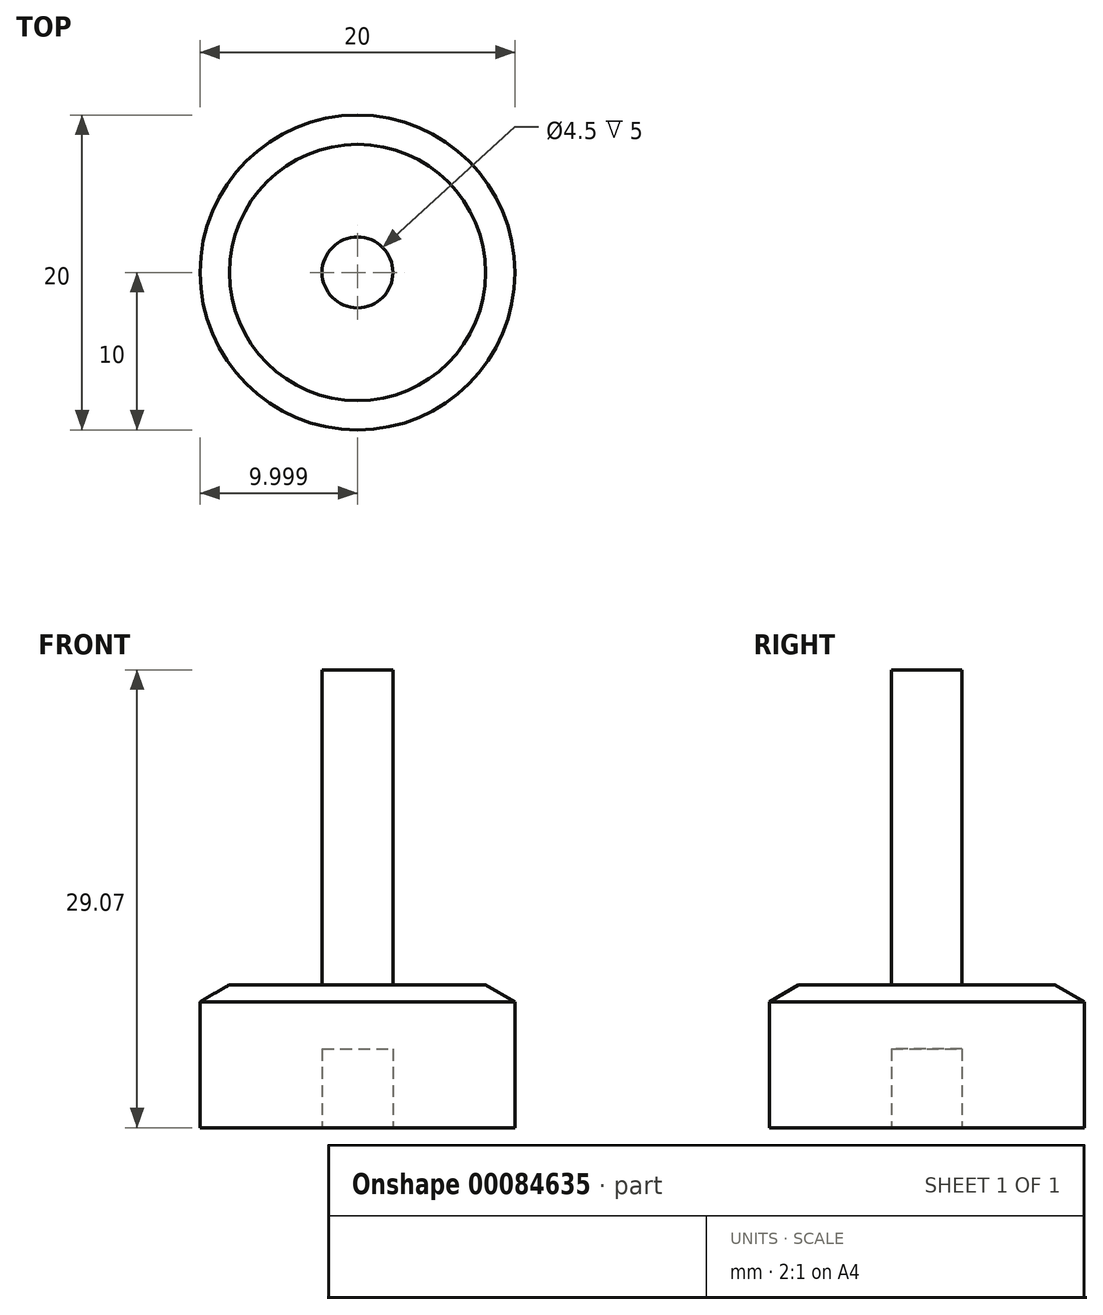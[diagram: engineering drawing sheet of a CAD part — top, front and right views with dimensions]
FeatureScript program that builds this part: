
annotation { "Feature Type Name" : "Feature", "Feature Type Description" : "" }
export const myFeature = defineFeature(function(context is Context, id is Id, definition is map)
    precondition{}
    {
        {
            var Q0;
            Q0=qCreatedBy(makeId("Front.planeOp"),FACE);
            var sketch = newSketch(context, id + "F0", { "sketchPlane" : qUnion([Q0])});
            skLineSegment(sketch, "E0.bottom", {"start": v(-30.55, 8) * mm, "end": v(-20.55, 8) * mm});
            skLineSegment(sketch, "E0.top", {"start": v(-30.55, 0) * mm, "end": v(-22.8, 0) * mm});
            skLineSegment(sketch, "E0.left", {"start": v(-30.55, 8) * mm, "end": v(-30.55, 0) * mm});
            skPoint(sketch, "E1", {"position": v(-20.55, 8) * mm});
            skPoint(sketch, "E2", {"position": v(-20.55, 0) * mm});
            skPoint(sketch, "E3", {"position": v(-20.55, 9.07) * mm});
            skLineSegment(sketch, "E4", {"start": v(-20.55, 8) * mm, "end": v(-20.55, 9.07) * mm});
            skLineSegment(sketch, "E5", {"start": v(-30.55, 8) * mm, "end": v(-28.7, 9.07) * mm});
            skLineSegment(sketch, "E6", {"start": v(-28.7, 9.07) * mm, "end": v(-20.55, 9.07) * mm});
            skLineSegment(sketch, "E7", {"start": v(-20.55, 8) * mm, "end": v(-20.55, 5) * mm});
            skPoint(sketch, "E0.right.end.orphan", {"position": v(-10.55, 0) * mm});
            skPoint(sketch, "E8.start.orphan", {"position": v(-10.55, 8) * mm});
            skLineSegment(sketch, "E9", {"start": v(-20.55, 9.07) * mm, "end": v(-20.55, 29.07) * mm});
            skLineSegment(sketch, "E10", {"start": v(-20.55, 29.07) * mm, "end": v(-22.8, 29.07) * mm});
            skLineSegment(sketch, "E11", {"start": v(-22.8, 29.07) * mm, "end": v(-22.8, 0) * mm});
            skPoint(sketch, "E12.start.orphan", {"position": v(-20.55, 4) * mm});
            skLineSegment(sketch, "E13", {"start": v(-20.55, 5) * mm, "end": v(-22.8, 5) * mm});
            skPoint(sketch, "E14", {"position": v(-20.55, 5) * mm});
            skSolve(sketch);
        }
        {
            var Q0;
            {var subQ0=sQuery(id+"F0.wireOp",EDGE,"E9");Q0=makeQuery(id+"F0.imprint","IMPRINT",FACE,{"disambiguationData":[TD([[makeQuery(id+"F0.imprint","IMPRINT",EDGE,{"derivedFrom":subQ0}),1.0]])]});}
            var Q1;
            {var subQ5=sQuery(id+"F0.wireOp",EDGE,"E0.top");Q1=makeQuery(id+"F0.imprint","IMPRINT",FACE,{"disambiguationData":[TD([[makeQuery(id+"F0.imprint","IMPRINT",EDGE,{"derivedFrom":subQ5}),1.0]])]});}
            var Q2;
            {var subQ0=sQuery(id+"F0.wireOp",EDGE,"E5");Q2=makeQuery(id+"F0.imprint","IMPRINT",FACE,{"disambiguationData":[TD([[makeQuery(id+"F0.imprint","IMPRINT",EDGE,{"derivedFrom":subQ0}),-1.0]])]});}
            var Q3;
            {var subQ0=sQuery(id+"F0.wireOp",EDGE,"E7");Q3=makeQuery(id+"F0.imprint","IMPRINT",FACE,{"disambiguationData":[TD([[makeQuery(id+"F0.imprint","IMPRINT",EDGE,{"derivedFrom":subQ0}),-1.0]])]});}
            var Q4;
            {var subQ0=sQuery(id+"F0.wireOp",EDGE,"E4");Q4=makeQuery(id+"F0.imprint","IMPRINT",FACE,{"disambiguationData":[TD([[makeQuery(id+"F0.imprint","IMPRINT",EDGE,{"derivedFrom":subQ0}),1.0]])]});}
            var Q5;
            Q5=sQuery(id+"F0.wireOp",EDGE,"E9");
            revolve(context, id + "F1", {"entities" : qUnion([Q0, Q1, Q2, Q3, Q4]), "axis" : qUnion([Q5]), "revolveType" : RevolveType.FULL});
        }
    });
